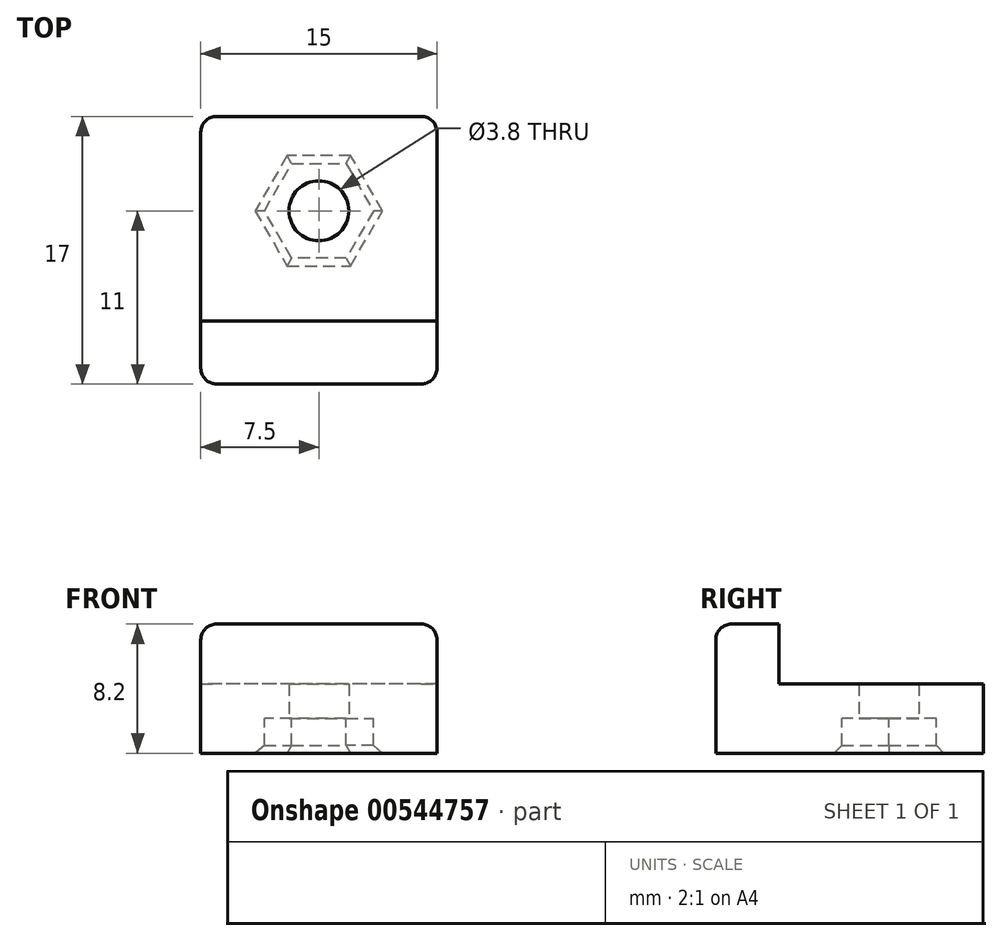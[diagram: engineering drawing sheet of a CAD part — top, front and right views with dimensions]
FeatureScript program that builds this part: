
annotation { "Feature Type Name" : "Feature", "Feature Type Description" : "" }
export const myFeature = defineFeature(function(context is Context, id is Id, definition is map)
    precondition{}
    {
        {
            var Q0;
            Q0=qCreatedBy(makeId("Top.planeOp"),FACE);
            var sketch = newSketch(context, id + "F0", { "sketchPlane" : qUnion([Q0])});
            skLineSegment(sketch, "E0.bottom", {"start": v(0, 0) * mm, "end": v(15, 0) * mm});
            skLineSegment(sketch, "E0.top", {"start": v(0, -17) * mm, "end": v(15, -17) * mm});
            skLineSegment(sketch, "E0.left", {"start": v(0, 0) * mm, "end": v(0, -17) * mm});
            skLineSegment(sketch, "E0.right", {"start": v(15, 0) * mm, "end": v(15, -17) * mm});
            skLineSegment(sketch, "E1", {"start": v(7.5, 0) * mm, "end": v(7.5, -17) * mm, "construction": true});
            skCircle(sketch, "E2.cCircle", {"center": v(7.5, -6) * mm, "radius": 3 * mm, "construction": true});
            skLineSegment(sketch, "E2.0", {"start": v(9.23, -3) * mm, "end": v(10.96, -6) * mm});
            skLineSegment(sketch, "E2.1", {"start": v(10.96, -6) * mm, "end": v(9.23, -9) * mm});
            skLineSegment(sketch, "E2.2", {"start": v(9.23, -9) * mm, "end": v(5.77, -9) * mm});
            skLineSegment(sketch, "E2.3", {"start": v(5.77, -9) * mm, "end": v(4.04, -6) * mm});
            skLineSegment(sketch, "E2.4", {"start": v(4.04, -6) * mm, "end": v(5.77, -3) * mm});
            skLineSegment(sketch, "E2.5", {"start": v(5.77, -3) * mm, "end": v(9.23, -3) * mm});
            skPoint(sketch, "E2.0.midPoint", {"position": v(10.1, -4.5) * mm});
            skLineSegment(sketch, "E3", {"start": v(0, -13) * mm, "end": v(15, -13) * mm});
            skCircle(sketch, "E4", {"center": v(7.5, -6) * mm, "radius": 1.9 * mm});
            skSolve(sketch);
        }
        {
            var Q0;
            Q0 = qSketchRegion(id + "F0", true);
            extrude(context, id + "F1", {"entities" : qUnion([Q0]), "depth" : 2.2 * mm, "offsetDistance" : 25 * mm});
        }
        {
            var Q0;
            {var subQ0=sQuery(id+"F0.wireOp",EDGE,"E0.top");Q0=makeQuery(id+"F0.imprint","IMPRINT",FACE,{"disambiguationData":[TD([[makeQuery(id+"F0.imprint","IMPRINT",EDGE,{"derivedFrom":subQ0}),1.0]])]});}
            extrude(context, id + "F2", {"entities" : qUnion([Q0]), "operationType" : NewBodyOperationType.ADD, "oppositeDirection" : true, "depth" : 6 * mm, "offsetDistance" : 25 * mm});
        }
        {
            var Q0;
            Q0=makeQuery(id+"F0.imprint","IMPRINT",FACE,{"disambiguationData":[TD([[makeQuery(id+"F0.imprint","IMPRINT",EDGE,{"derivedFrom":sQuery(id+"F0.wireOp",EDGE,"E2.0")}),-1.0]])]});
            var Q1;
            {var subQ1=sQuery(id+"F0.wireOp",EDGE,"E0.bottom");Q1=makeQuery(id+"F0.imprint","IMPRINT",FACE,{"disambiguationData":[TD([[makeQuery(id+"F0.imprint","IMPRINT",EDGE,{"derivedFrom":subQ1}),-1.0]])]});}
            extrude(context, id + "F3", {"entities" : qUnion([Q0, Q1]), "operationType" : NewBodyOperationType.ADD, "oppositeDirection" : true, "depth" : 2.2 * mm, "offsetDistance" : 25 * mm});
        }
        {
            var Q0;
            {var subQ0=sQuery(id+"F0.wireOp",EDGE,"E0.left");var subQ1=sQuery(id+"F0.wireOp",EDGE,"E0.bottom");Q0=makeQuery(id+"F3.boolean.opBoolean","MERGE",EDGE,{"derivedFrom":[makeQuery(id+"F1.opExtrude","SWEPT_EDGE",EDGE,{"disambiguationData":[OSD([subQ1,subQ0])]}),makeQuery(id+"F3.opExtrude","SWEPT_EDGE",EDGE,{"disambiguationData":[OSD([subQ1,subQ0])]})]});}
            var Q1;
            {var subQ0=sQuery(id+"F0.wireOp",EDGE,"E0.right");var subQ1=sQuery(id+"F0.wireOp",EDGE,"E0.bottom");Q1=makeQuery(id+"F3.boolean.opBoolean","MERGE",EDGE,{"derivedFrom":[makeQuery(id+"F1.opExtrude","SWEPT_EDGE",EDGE,{"disambiguationData":[OSD([subQ1,subQ0])]}),makeQuery(id+"F3.opExtrude","SWEPT_EDGE",EDGE,{"disambiguationData":[OSD([subQ1,subQ0])]})]});}
            var Q2;
            {var subQ0=sQuery(id+"F0.wireOp",EDGE,"E0.left");var subQ1=sQuery(id+"F0.wireOp",EDGE,"E0.top");Q2=makeQuery(id+"F2.boolean.opBoolean","MERGE",EDGE,{"derivedFrom":[makeQuery(id+"F1.opExtrude","SWEPT_EDGE",EDGE,{"disambiguationData":[OSD([subQ1,subQ0])]}),makeQuery(id+"F2.opExtrude","SWEPT_EDGE",EDGE,{"disambiguationData":[OSD([subQ1,subQ0])]})]});}
            var Q3;
            {var subQ0=sQuery(id+"F0.wireOp",EDGE,"E0.right");var subQ1=sQuery(id+"F0.wireOp",EDGE,"E0.top");Q3=makeQuery(id+"F2.boolean.opBoolean","MERGE",EDGE,{"derivedFrom":[makeQuery(id+"F1.opExtrude","SWEPT_EDGE",EDGE,{"disambiguationData":[OSD([subQ1,subQ0])]}),makeQuery(id+"F2.opExtrude","SWEPT_EDGE",EDGE,{"disambiguationData":[OSD([subQ1,subQ0])]})]});}
            var Q4;
            Q4=makeQuery(id+"F2.opExtrude","CAP_EDGE",EDGE,{"disambiguationData":[OSD([sQuery(id+"F0.wireOp",EDGE,"E0.top")])],"isStart":false});
            var Q5;
            Q5=makeQuery(id+"F2.opExtrude","CAP_EDGE",EDGE,{"disambiguationData":[OSD([sQuery(id+"F0.wireOp",EDGE,"E0.right")])],"isStart":false});
            var Q6;
            Q6=makeQuery(id+"F2.opExtrude","CAP_EDGE",EDGE,{"disambiguationData":[OSD([sQuery(id+"F0.wireOp",EDGE,"E0.left")])],"isStart":false});
            fillet(context, id + "F4", {"entities" : qUnion([Q0, Q1, Q2, Q3, Q4, Q5, Q6]), "radius" : 1 * mm, "tangentPropagation" : true, "allowEdgeOverflow" : false});
        }
        {
            var Q0;
            Q0=makeQuery(id+"F1.opExtrude","SWEPT_BODY",BODY,{"disambiguationData":[OSD([sQuery(id+"F0.wireOp",EDGE,"E0.bottom"),sQuery(id+"F0.wireOp",EDGE,"E0.top"),sQuery(id+"F0.wireOp",EDGE,"E0.left"),sQuery(id+"F0.wireOp",EDGE,"E0.right"),sQuery(id+"F0.wireOp",EDGE,"E2.0"),sQuery(id+"F0.wireOp",EDGE,"E2.1"),sQuery(id+"F0.wireOp",EDGE,"E2.2"),sQuery(id+"F0.wireOp",EDGE,"E2.3"),sQuery(id+"F0.wireOp",EDGE,"E2.4"),sQuery(id+"F0.wireOp",EDGE,"E2.5")])]});
            var Q1;
            Q1=makeQuery(id+"F1.opExtrude","CAP_EDGE",EDGE,{"disambiguationData":[OSD([sQuery(id+"F0.wireOp",EDGE,"E0.left")])],"isStart":false});
            transform(context, id + "F5", {"entities" : qUnion([Q0]), "transformType" : TransformType.ROTATION, "transformAxis" : qUnion([Q1]), "angle" : 180 * degree, "makeCopy" : false});
        }
        {
            var Q0;
            Q0=makeQuery(id+"F1.opExtrude","CAP_EDGE",EDGE,{"disambiguationData":[OSD([sQuery(id+"F0.wireOp",EDGE,"E2.4")])],"isStart":false});
            var Q1;
            Q1=makeQuery(id+"F1.opExtrude","CAP_EDGE",EDGE,{"disambiguationData":[OSD([sQuery(id+"F0.wireOp",EDGE,"E2.5")])],"isStart":false});
            var Q2;
            Q2=makeQuery(id+"F1.opExtrude","CAP_EDGE",EDGE,{"disambiguationData":[OSD([sQuery(id+"F0.wireOp",EDGE,"E2.0")])],"isStart":false});
            var Q3;
            Q3=makeQuery(id+"F1.opExtrude","CAP_EDGE",EDGE,{"disambiguationData":[OSD([sQuery(id+"F0.wireOp",EDGE,"E2.1")])],"isStart":false});
            var Q4;
            Q4=makeQuery(id+"F1.opExtrude","CAP_EDGE",EDGE,{"disambiguationData":[OSD([sQuery(id+"F0.wireOp",EDGE,"E2.2")])],"isStart":false});
            var Q5;
            Q5=makeQuery(id+"F1.opExtrude","CAP_EDGE",EDGE,{"disambiguationData":[OSD([sQuery(id+"F0.wireOp",EDGE,"E2.3")])],"isStart":false});
            chamfer(context, id + "F6", {"entities" : qUnion([Q0, Q1, Q2, Q3, Q4, Q5]), "width" : 0.5 * mm, "tangentPropagation" : true});
        }
    });
